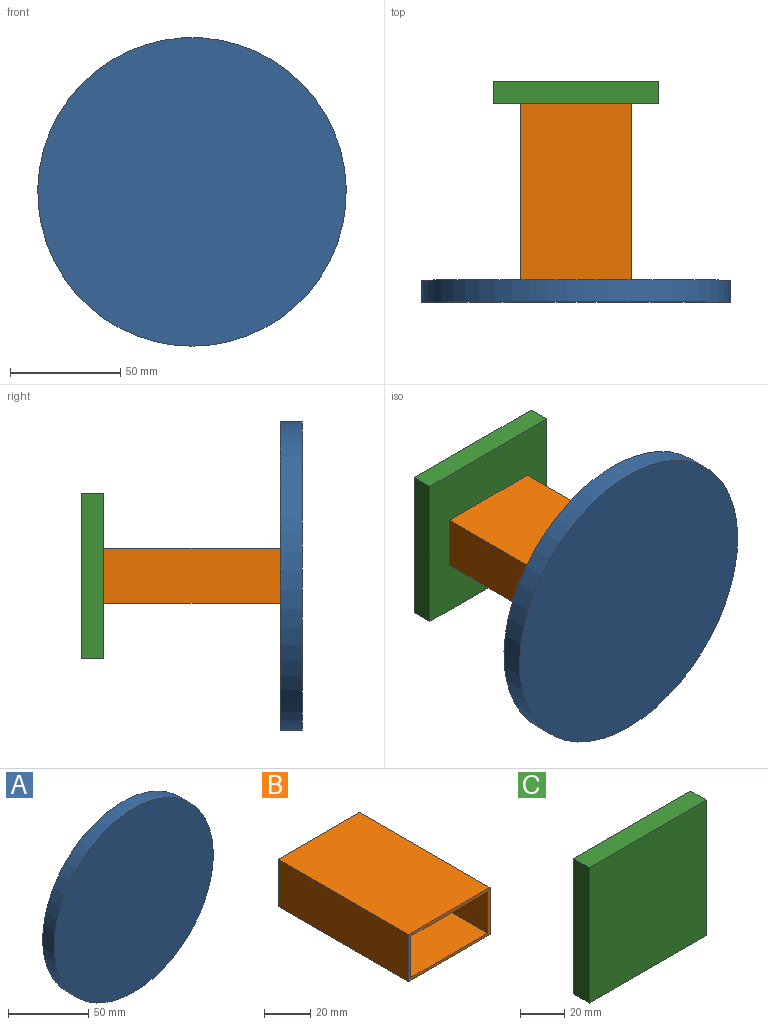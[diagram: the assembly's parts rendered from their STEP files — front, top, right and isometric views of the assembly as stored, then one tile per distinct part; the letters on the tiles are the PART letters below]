
ASSEMBLY  parts=3 mates=2
PART A: 3 faces, bbox 140x10x140 mm
  f0: cylinder r=70mm len=140mm, axis (0,-1,0), area 4398.2mm2, adj f1,f2
  f1: plane 140x140mm, normal (0,1,0), area 15393.8mm2, adj f0
  f2: plane 140x140mm, normal (0,-1,0), area 15393.8mm2, adj f0
PART B: 10 faces, bbox 50x80x25 mm
  f0: plane 80x47mm, normal (0,0,1), area 3760mm2, adj f1,f7,f8,f9
  f1: plane 80x22mm, normal (1,0,0), area 1760mm2, adj f0,f2,f8,f9
  f2: plane 80x47mm, normal (0,0,-1), area 3760mm2, adj f1,f7,f8,f9
  f3: plane 80x25mm, normal (-1,0,0), area 2000mm2, adj f4,f6,f8,f9
  f4: plane 80x50mm, normal (0,0,-1), area 4000mm2, adj f3,f5,f8,f9
  f5: plane 80x25mm, normal (1,0,0), area 2000mm2, adj f4,f6,f8,f9
  f6: plane 80x50mm, normal (0,0,1), area 4000mm2, adj f3,f5,f8,f9
  f7: plane 80x22mm, normal (-1,0,0), area 1760mm2, adj f0,f2,f8,f9
  f8: plane 50x25mm, normal (0,-1,0), area 216mm2, adj f0,f1,f2,f3,f4,f5,f6,f7
  f9: plane 50x25mm, normal (0,1,0), area 216mm2, adj f0,f1,f2,f3,f4,f5,f6,f7
PART C: 6 faces, bbox 75x10x75 mm
  f0: plane 75x10mm, normal (0,0,1), area 750mm2, adj f1,f3,f4,f5
  f1: plane 75x10mm, normal (-1,0,0), area 750mm2, adj f0,f2,f4,f5
  f2: plane 75x10mm, normal (0,0,-1), area 750mm2, adj f1,f3,f4,f5
  f3: plane 75x10mm, normal (1,0,0), area 750mm2, adj f0,f2,f4,f5
  f4: plane 75x75mm, normal (0,-1,0), area 5625mm2, adj f0,f1,f2,f3
  f5: plane 75x75mm, normal (0,1,0), area 5625mm2, adj f0,f1,f2,f3
PLACE A t=(3.96,-108.3,-65.48)mm
PLACE B t=(3.96,-63.3,-65.48)mm
PLACE C t=(3.96,-18.3,-65.48)mm fixed
MATE fastened C.f4 <-> B.f9  axis (0,-1,0) through (3.96,-23.3,-65.48)mm
MATE fastened A.f0 <-> B.f8  axis (0,1,0) through (3.96,-103.3,-65.48)mm
